# Revit family: Showerhead-DXV-Slim_Rectangle_D35700412_Series
name_source: partatom
category: Plumbing Fixtures
revit_build: Autodesk Revit 2014 (Build: 20130308_1515(x64)
units: mm (PartAtom-declared; Revit-internal decimal feet)

## types (1)
- D35700412.100
    Assembly Code = D2010710
    CW Connection = Yes
    CWFU = 3
    Default Elevation = 0"
    Description = Slim Rectangle 12 Inch Showerhead Contemporary Accents Collection
    Finish = Brass-DXV-100-Polished Chrome
    Flow Rate = 2.5 gpm.  (9.5 L/min.)
    HW Connection = Yes
    HWFU = 3
    Length = 11 13/16"
    Manufacturer = DXV
    Material = Brass-DXV-100-Polished Chrome
    Model = D35700412.100
    Price = Prices may vary. Please consult Manufacturer Representative for most up-to-date price list.
    Product Documentation Link = https://dxv01.blob.core.windows.net
    Product Page URL = https://www.dxv.com
    URL = https://www.dxv.com
    Vent Connection = No
    WFU = 4
    Warranty Documentation Link = https://www.dxv.com
    Waste Connection = Yes
    Water Connection Diameter = 1/2"
    Width = 7 7/8"

## geometry (parser evidence)
native form markers: Sweep x3
no freeform markers — native parametric forms only
